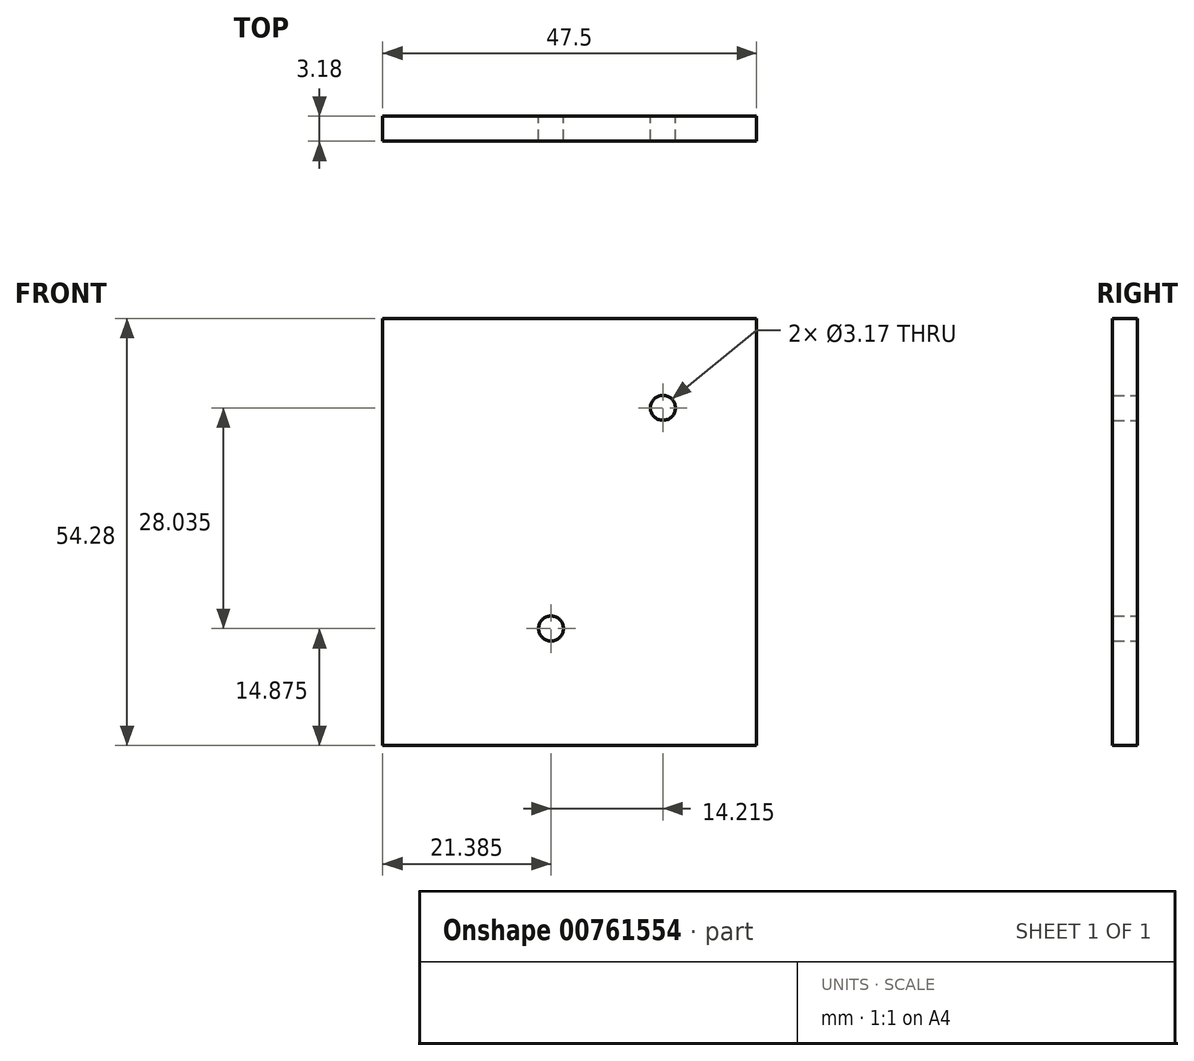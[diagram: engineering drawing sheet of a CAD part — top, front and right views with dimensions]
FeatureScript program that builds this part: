
annotation { "Feature Type Name" : "Feature", "Feature Type Description" : "" }
export const myFeature = defineFeature(function(context is Context, id is Id, definition is map)
    precondition{}
    {
        {
            var Q0;
            Q0=qCreatedBy(makeId("Front.planeOp"),FACE);
            var sketch = newSketch(context, id + "F0", { "sketchPlane" : qUnion([Q0])});
            skLineSegment(sketch, "E0.bottom", {"start": v(-37.2, -6.02) * mm, "end": v(0.9, -6.02) * mm});
            skLineSegment(sketch, "E0.top", {"start": v(-37.2, -56.82) * mm, "end": v(0.9, -56.82) * mm});
            skLineSegment(sketch, "E0.left", {"start": v(-37.2, -6.02) * mm, "end": v(-37.2, -50.47) * mm});
            skLineSegment(sketch, "E0.right", {"start": v(0.9, -6.02) * mm, "end": v(0.9, -50.47) * mm});
            skCircle(sketch, "E1", {"center": v(-8.97, -18.31) * mm, "radius": 8.03 * mm});
            skCircle(sketch, "E2", {"center": v(-20.88, -38.12) * mm, "radius": 15.09 * mm});
            skCircle(sketch, "E3", {"center": v(-20.88, -38.12) * mm, "radius": 1.59 * mm});
            skCircle(sketch, "E4", {"center": v(-8.97, -18.31) * mm, "radius": 1.59 * mm});
            skLineSegment(sketch, "E5.bottom", {"start": v(0.9, -56.82) * mm, "end": v(4.46, -56.82) * mm});
            skLineSegment(sketch, "E5.top", {"start": v(3.44, -53) * mm, "end": v(4.46, -53) * mm});
            skLineSegment(sketch, "E5.right", {"start": v(4.46, -56.82) * mm, "end": v(4.46, -53) * mm});
            skLineSegment(sketch, "E6.bottom", {"start": v(-37.2, -56.82) * mm, "end": v(-40.76, -56.82) * mm});
            skLineSegment(sketch, "E6.top", {"start": v(-39.74, -53) * mm, "end": v(-40.76, -53) * mm});
            skLineSegment(sketch, "E6.right", {"start": v(-40.76, -56.82) * mm, "end": v(-40.76, -53) * mm});
            skPoint(sketch, "E7.visualSharp", {"position": v(-37.2, -53) * mm});
            skArc(sketch, "E7.filletArc", {"start": v(-39.74, -53) * mm, "mid": v(-37.94, -52.27) * mm, "end": v(-37.2, -50.47) * mm});
            skPoint(sketch, "E8.visualSharp", {"position": v(0.9, -53) * mm});
            skArc(sketch, "E8.filletArc", {"start": v(0.9, -50.47) * mm, "mid": v(1.64, -52.27) * mm, "end": v(3.44, -53) * mm});
            skCircle(sketch, "E9", {"center": v(50.4, 38.83) * mm, "radius": 10.8 * mm});
            skCircle(sketch, "E10", {"center": v(50.4, 38.83) * mm, "radius": 1.59 * mm});
            skCircle(sketch, "E11", {"center": v(36.2, 10.8) * mm, "radius": 20.64 * mm});
            skCircle(sketch, "E12", {"center": v(36.2, 10.8) * mm, "radius": 1.59 * mm});
            skLineSegment(sketch, "E13.filletArc", {"start": v(62.96, -5.77) * mm, "end": v(62.96, -5.77) * mm});
            skLineSegment(sketch, "E14.filletArc", {"start": v(12.16, -5.77) * mm, "end": v(12.16, -5.77) * mm});
            skLineSegment(sketch, "E15.bottom", {"start": v(62.3, 50.2) * mm, "end": v(14.8, 50.2) * mm});
            skLineSegment(sketch, "E15.top", {"start": v(62.3, -4.08) * mm, "end": v(14.8, -4.08) * mm});
            skLineSegment(sketch, "E15.left", {"start": v(62.3, 50.2) * mm, "end": v(62.3, -4.08) * mm});
            skLineSegment(sketch, "E15.right", {"start": v(14.8, 50.2) * mm, "end": v(14.8, -4.08) * mm});
            skSolve(sketch);
        }
        {
            var Q0;
            Q0=makeQuery(id+"F0.imprint","IMPRINT",FACE,{"disambiguationData":[TD([[makeQuery(id+"F0.imprint","IMPRINT",EDGE,{"derivedFrom":sQuery(id+"F0.wireOp",EDGE,"E11")}),1.0]])]});
            var Q1;
            Q1=makeQuery(id+"F0.imprint","IMPRINT",FACE,{"disambiguationData":[TD([[makeQuery(id+"F0.imprint","IMPRINT",EDGE,{"derivedFrom":sQuery(id+"F0.wireOp",EDGE,"E9")}),-1.0]])]});
            var Q2;
            Q2=makeQuery(id+"F0.imprint","IMPRINT",FACE,{"disambiguationData":[TD([[makeQuery(id+"F0.imprint","IMPRINT",EDGE,{"derivedFrom":sQuery(id+"F0.wireOp",EDGE,"E9")}),1.0]])]});
            extrude(context, id + "F1", {"entities" : qUnion([Q0, Q1, Q2]), "depth" : 3.17 * mm, "offsetDistance" : 25.4 * mm});
        }
    });
